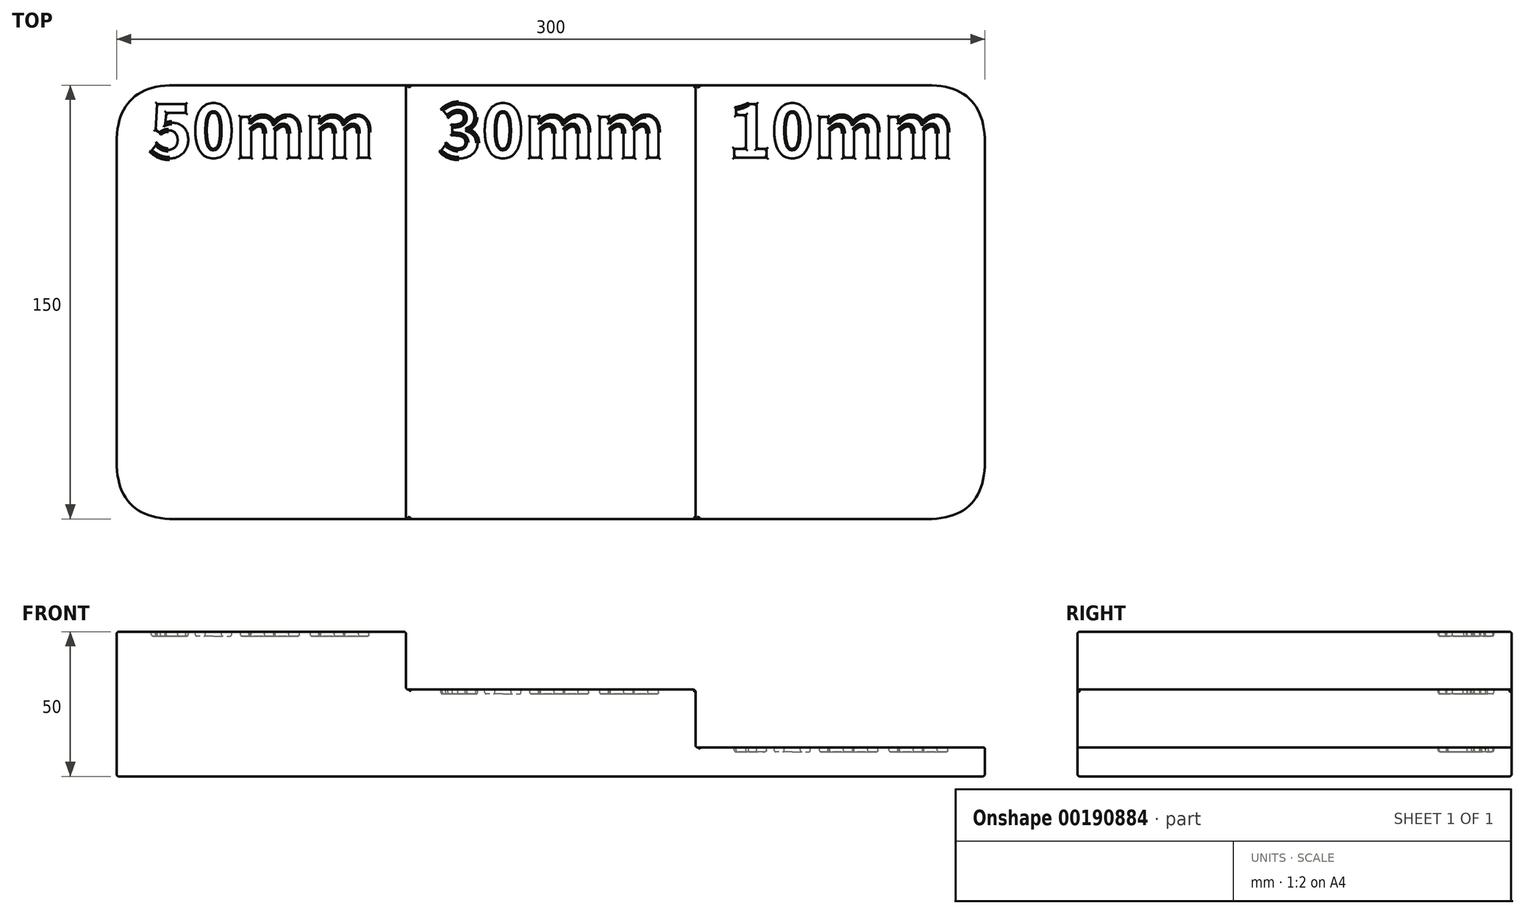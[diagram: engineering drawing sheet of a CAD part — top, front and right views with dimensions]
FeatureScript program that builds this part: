
annotation { "Feature Type Name" : "Feature", "Feature Type Description" : "" }
export const myFeature = defineFeature(function(context is Context, id is Id, definition is map)
    precondition{}
    {
        {
            var Q0;
            Q0=qCreatedBy(makeId("Top.planeOp"),FACE);
            var sketch = newSketch(context, id + "F0", { "sketchPlane" : qUnion([Q0])});
            skLineSegment(sketch, "E0.bottom", {"start": v(150, 75) * mm, "end": v(-150, 75) * mm});
            skLineSegment(sketch, "E0.top", {"start": v(150, -75) * mm, "end": v(-150, -75) * mm});
            skLineSegment(sketch, "E0.left", {"start": v(150, 75) * mm, "end": v(150, -75) * mm});
            skLineSegment(sketch, "E0.right", {"start": v(-150, 75) * mm, "end": v(-150, -75) * mm});
            skPoint(sketch, "E0.middle", {"position": v(0, 0) * mm});
            skLineSegment(sketch, "E1", {"start": v(-150, 0) * mm, "end": v(-50, 0) * mm, "construction": true});
            skLineSegment(sketch, "E2", {"start": v(-50, 0) * mm, "end": v(50, 0) * mm, "construction": true});
            skLineSegment(sketch, "E3", {"start": v(50, 0) * mm, "end": v(150, 0) * mm, "construction": true});
            skLineSegment(sketch, "E4", {"start": v(-50, 75) * mm, "end": v(-50, -75) * mm});
            skLineSegment(sketch, "E5", {"start": v(50, 75) * mm, "end": v(50, -75) * mm});
            skSolve(sketch);
        }
        {
            var Q0;
            Q0 = qSketchRegion(id + "F0", true);
            extrude(context, id + "F1", {"entities" : qUnion([Q0]), "depth" : 10 * mm});
        }
        {
            var Q0;
            {var subQ0=sQuery(id+"F0.wireOp",EDGE,"E4");Q0=makeQuery(id+"F0.imprint","IMPRINT",FACE,{"disambiguationData":[TD([[makeQuery(id+"F0.imprint","IMPRINT",EDGE,{"derivedFrom":subQ0}),1.0]])]});}
            var Q1;
            {var subQ0=sQuery(id+"F0.wireOp",EDGE,"E0.right");Q1=makeQuery(id+"F0.imprint","IMPRINT",FACE,{"disambiguationData":[TD([[makeQuery(id+"F0.imprint","IMPRINT",EDGE,{"derivedFrom":subQ0}),1.0]])]});}
            extrude(context, id + "F2", {"entities" : qUnion([Q0, Q1]), "operationType" : NewBodyOperationType.ADD, "depth" : 30 * mm});
        }
        {
            var Q0;
            {var subQ0=sQuery(id+"F0.wireOp",EDGE,"E0.right");Q0=makeQuery(id+"F0.imprint","IMPRINT",FACE,{"disambiguationData":[TD([[makeQuery(id+"F0.imprint","IMPRINT",EDGE,{"derivedFrom":subQ0}),1.0]])]});}
            extrude(context, id + "F3", {"entities" : qUnion([Q0]), "operationType" : NewBodyOperationType.ADD, "depth" : 50 * mm});
        }
        {
            var Q0;
            {var subQ0=sQuery(id+"F0.wireOp",EDGE,"E0.right");var subQ1=sQuery(id+"F0.wireOp",EDGE,"E0.bottom");Q0=makeQuery(id+"F3.boolean.opBoolean","MERGE",EDGE,{"derivedFrom":[makeQuery(id+"F2.boolean.opBoolean","MERGE",EDGE,{"derivedFrom":[makeQuery(id+"F1.opExtrude","SWEPT_EDGE",EDGE,{"disambiguationData":[OSD([subQ1,subQ0])]}),makeQuery(id+"F2.opExtrude","SWEPT_EDGE",EDGE,{"disambiguationData":[OSD([subQ1,subQ0])]})]}),makeQuery(id+"F3.opExtrude","SWEPT_EDGE",EDGE,{"disambiguationData":[OSD([subQ1,subQ0])]})]});}
            var Q1;
            {var subQ0=sQuery(id+"F0.wireOp",EDGE,"E0.right");var subQ1=sQuery(id+"F0.wireOp",EDGE,"E0.top");Q1=makeQuery(id+"F3.boolean.opBoolean","MERGE",EDGE,{"derivedFrom":[makeQuery(id+"F2.boolean.opBoolean","MERGE",EDGE,{"derivedFrom":[makeQuery(id+"F1.opExtrude","SWEPT_EDGE",EDGE,{"disambiguationData":[OSD([subQ1,subQ0])]}),makeQuery(id+"F2.opExtrude","SWEPT_EDGE",EDGE,{"disambiguationData":[OSD([subQ1,subQ0])]})]}),makeQuery(id+"F3.opExtrude","SWEPT_EDGE",EDGE,{"disambiguationData":[OSD([subQ1,subQ0])]})]});}
            var Q2;
            Q2=makeQuery(id+"F1.opExtrude","SWEPT_EDGE",EDGE,{"disambiguationData":[OSD([sQuery(id+"F0.wireOp",EDGE,"E0.top"),sQuery(id+"F0.wireOp",EDGE,"E0.left")])]});
            var Q3;
            Q3=makeQuery(id+"F1.opExtrude","SWEPT_EDGE",EDGE,{"disambiguationData":[OSD([sQuery(id+"F0.wireOp",EDGE,"E0.bottom"),sQuery(id+"F0.wireOp",EDGE,"E0.left")])]});
            fillet(context, id + "F4", {"entities" : qUnion([Q0, Q1, Q2, Q3]), "radius" : 20 * mm, "tangentPropagation" : true, "rho" : 0.5, "crossSection" : FilletCrossSection.CONIC, "allowEdgeOverflow" : false});
        }
        {
            var Q0;
            {var subQ0=sQuery(id+"F0.wireOp",EDGE,"E0.right");Q0=makeQuery(id+"F3.boolean.opBoolean","MERGE",FACE,{"derivedFrom":[makeQuery(id+"F2.boolean.opBoolean","MERGE",FACE,{"derivedFrom":[makeQuery(id+"F1.opExtrude","SWEPT_FACE",FACE,{"disambiguationData":[OSD([subQ0])]}),makeQuery(id+"F2.opExtrude","SWEPT_FACE",FACE,{"disambiguationData":[OSD([subQ0])]})]}),makeQuery(id+"F3.opExtrude","SWEPT_FACE",FACE,{"disambiguationData":[OSD([subQ0])]})]});}
            var Q1;
            Q1=makeQuery(id+"F3.opExtrude","SWEPT_FACE",FACE,{"disambiguationData":[OSD([sQuery(id+"F0.wireOp",EDGE,"E4")])]});
            var Q2;
            Q2=makeQuery(id+"F2.opExtrude","SWEPT_FACE",FACE,{"disambiguationData":[OSD([sQuery(id+"F0.wireOp",EDGE,"E5")])]});
            fillet(context, id + "F5", {"entities" : qUnion([Q0, Q1, Q2]), "radius" : 0.75 * mm, "tangentPropagation" : true, "allowEdgeOverflow" : false});
        }
        {
            var Q0;
            Q0=makeQuery(id+"F1.opExtrude","CAP_FACE",FACE,{"disambiguationData":[OSD([sQuery(id+"F0.wireOp",EDGE,"E0.bottom"),sQuery(id+"F0.wireOp",EDGE,"E0.top"),sQuery(id+"F0.wireOp",EDGE,"E0.left"),sQuery(id+"F0.wireOp",EDGE,"E0.right")])],"isStart":false});
            var sketch = newSketch(context, id + "F6", { "sketchPlane" : qUnion([Q0])});
            skText(sketch, "E6", { "text": "10mm", "fontName": "NotoSansCJKsc-Bold.otf"});
            skPoint(sketch, "E7", {"position": v(100, 0) * mm});
            const initialGuessF6  = {"E6": [0.06138, 0.05, 1, 0, 0.018]};
            skSetInitialGuess(sketch, initialGuessF6);
            skSolve(sketch);
        }
        {
            var Q0;
            Q0=makeQuery(id+"F2.opExtrude","CAP_FACE",FACE,{"disambiguationData":[OSD([sQuery(id+"F0.wireOp",EDGE,"E0.bottom"),sQuery(id+"F0.wireOp",EDGE,"E0.top"),sQuery(id+"F0.wireOp",EDGE,"E0.right"),sQuery(id+"F0.wireOp",EDGE,"E5")])],"isStart":false});
            var sketch = newSketch(context, id + "F7", { "sketchPlane" : qUnion([Q0])});
            skText(sketch, "E8", { "text": "30mm", "fontName": "NotoSansCJKsc-Bold.otf"});
            skPoint(sketch, "E9", {"position": v(0, 0) * mm});
            const initialGuessF7  = {"E8": [-0.03862, 0.05, 1, 0, 0.018]};
            skSetInitialGuess(sketch, initialGuessF7);
            skSolve(sketch);
        }
        {
            var Q0;
            Q0=makeQuery(id+"F3.opExtrude","CAP_FACE",FACE,{"disambiguationData":[OSD([sQuery(id+"F0.wireOp",EDGE,"E0.bottom"),sQuery(id+"F0.wireOp",EDGE,"E0.top"),sQuery(id+"F0.wireOp",EDGE,"E0.right"),sQuery(id+"F0.wireOp",EDGE,"E4")])],"isStart":false});
            var sketch = newSketch(context, id + "F8", { "sketchPlane" : qUnion([Q0])});
            skText(sketch, "E10", { "text": "50mm", "fontName": "NotoSansCJKsc-Bold.otf"});
            skPoint(sketch, "E11", {"position": v(-100, 0) * mm});
            const initialGuessF8  = {"E10": [-0.13862, 0.05, 1, 0, 0.018]};
            skSetInitialGuess(sketch, initialGuessF8);
            skSolve(sketch);
        }
        {
            var Q0;
            Q0 = qSketchRegion(id + "F6", true);
            var Q1;
            Q1 = qSketchRegion(id + "F7", true);
            var Q2;
            Q2 = qSketchRegion(id + "F8", true);
            extrude(context, id + "F9", {"entities" : qUnion([Q0, Q1, Q2]), "operationType" : NewBodyOperationType.REMOVE, "oppositeDirection" : true, "depth" : 1.5 * mm});
        }
        {
            var Q0;
            {var subQ0=sQuery(id+"F0.wireOp",EDGE,"E0.right");var subQ1=sQuery(id+"F0.wireOp",EDGE,"E0.left");var subQ2=sQuery(id+"F0.wireOp",EDGE,"E0.top");var subQ3=sQuery(id+"F0.wireOp",EDGE,"E0.bottom");var subQ4=makeQuery(id+"F1.opExtrude","CAP_FACE",FACE,{"disambiguationData":[OSD([subQ3,subQ2,subQ1,subQ0])],"isStart":false});var subQ5=subQ4;Q0=makeQuery(id+"F9.boolean.opBoolean","SPLIT",FACE,{"disambiguationData":[TD([makeQuery(id+"F9.opExtrude","SWEPT_FACE",FACE,{"disambiguationData":[OSD([sQuery(id+"F6.wireOp",EDGE,"E6.sketch_text.stroke-0")])]})])],"derivedFrom":subQ5});}
            var Q1;
            Q1=makeQuery(id+"F9.boolean.opBoolean","SPLIT",FACE,{"disambiguationData":[TD([makeQuery(id+"F9.opExtrude","SWEPT_FACE",FACE,{"disambiguationData":[OSD([sQuery(id+"F6.wireOp",EDGE,"E6.sketch_text.stroke-15")])]})])],"derivedFrom":makeQuery(id+"F1.opExtrude","CAP_FACE",FACE,{"disambiguationData":[OSD([sQuery(id+"F0.wireOp",EDGE,"E0.bottom"),sQuery(id+"F0.wireOp",EDGE,"E0.top"),sQuery(id+"F0.wireOp",EDGE,"E0.left"),sQuery(id+"F0.wireOp",EDGE,"E0.right")])],"isStart":false})});
            var Q2;
            Q2=makeQuery(id+"F9.boolean.opBoolean","COPY",FACE,{"derivedFrom":makeQuery(id+"F9.opExtrude","CAP_FACE",FACE,{"disambiguationData":[OSD([sQuery(id+"F6.wireOp",EDGE,"E6.sketch_text.stroke-0"),sQuery(id+"F6.wireOp",EDGE,"E6.sketch_text.stroke-1"),sQuery(id+"F6.wireOp",EDGE,"E6.sketch_text.stroke-2"),sQuery(id+"F6.wireOp",EDGE,"E6.sketch_text.stroke-3"),sQuery(id+"F6.wireOp",EDGE,"E6.sketch_text.stroke-4"),sQuery(id+"F6.wireOp",EDGE,"E6.sketch_text.stroke-5"),sQuery(id+"F6.wireOp",EDGE,"E6.sketch_text.stroke-6"),sQuery(id+"F6.wireOp",EDGE,"E6.sketch_text.stroke-7"),sQuery(id+"F6.wireOp",EDGE,"E6.sketch_text.stroke-8"),sQuery(id+"F6.wireOp",EDGE,"E6.sketch_text.stroke-9"),sQuery(id+"F6.wireOp",EDGE,"E6.sketch_text.stroke-10")])],"isStart":false})});
            var Q3;
            Q3=makeQuery(id+"F9.boolean.opBoolean","COPY",FACE,{"derivedFrom":makeQuery(id+"F9.opExtrude","CAP_FACE",FACE,{"disambiguationData":[OSD([sQuery(id+"F6.wireOp",EDGE,"E6.sketch_text.stroke-11"),sQuery(id+"F6.wireOp",EDGE,"E6.sketch_text.stroke-12"),sQuery(id+"F6.wireOp",EDGE,"E6.sketch_text.stroke-13"),sQuery(id+"F6.wireOp",EDGE,"E6.sketch_text.stroke-14"),sQuery(id+"F6.wireOp",EDGE,"E6.sketch_text.stroke-15"),sQuery(id+"F6.wireOp",EDGE,"E6.sketch_text.stroke-16"),sQuery(id+"F6.wireOp",EDGE,"E6.sketch_text.stroke-17"),sQuery(id+"F6.wireOp",EDGE,"E6.sketch_text.stroke-18")])],"isStart":false})});
            var Q4;
            Q4=makeQuery(id+"F9.boolean.opBoolean","COPY",FACE,{"derivedFrom":makeQuery(id+"F9.opExtrude","CAP_FACE",FACE,{"disambiguationData":[OSD([sQuery(id+"F6.wireOp",EDGE,"E6.sketch_text.stroke-19"),sQuery(id+"F6.wireOp",EDGE,"E6.sketch_text.stroke-20"),sQuery(id+"F6.wireOp",EDGE,"E6.sketch_text.stroke-21"),sQuery(id+"F6.wireOp",EDGE,"E6.sketch_text.stroke-22"),sQuery(id+"F6.wireOp",EDGE,"E6.sketch_text.stroke-23"),sQuery(id+"F6.wireOp",EDGE,"E6.sketch_text.stroke-24"),sQuery(id+"F6.wireOp",EDGE,"E6.sketch_text.stroke-25"),sQuery(id+"F6.wireOp",EDGE,"E6.sketch_text.stroke-26"),sQuery(id+"F6.wireOp",EDGE,"E6.sketch_text.stroke-27"),sQuery(id+"F6.wireOp",EDGE,"E6.sketch_text.stroke-28"),sQuery(id+"F6.wireOp",EDGE,"E6.sketch_text.stroke-29"),sQuery(id+"F6.wireOp",EDGE,"E6.sketch_text.stroke-30"),sQuery(id+"F6.wireOp",EDGE,"E6.sketch_text.stroke-31"),sQuery(id+"F6.wireOp",EDGE,"E6.sketch_text.stroke-32"),sQuery(id+"F6.wireOp",EDGE,"E6.sketch_text.stroke-33"),sQuery(id+"F6.wireOp",EDGE,"E6.sketch_text.stroke-34"),sQuery(id+"F6.wireOp",EDGE,"E6.sketch_text.stroke-35"),sQuery(id+"F6.wireOp",EDGE,"E6.sketch_text.stroke-36"),sQuery(id+"F6.wireOp",EDGE,"E6.sketch_text.stroke-37"),sQuery(id+"F6.wireOp",EDGE,"E6.sketch_text.stroke-38")])],"isStart":false})});
            var Q5;
            Q5=makeQuery(id+"F9.boolean.opBoolean","COPY",FACE,{"derivedFrom":makeQuery(id+"F9.opExtrude","CAP_FACE",FACE,{"disambiguationData":[OSD([sQuery(id+"F6.wireOp",EDGE,"E6.sketch_text.stroke-39"),sQuery(id+"F6.wireOp",EDGE,"E6.sketch_text.stroke-40"),sQuery(id+"F6.wireOp",EDGE,"E6.sketch_text.stroke-41"),sQuery(id+"F6.wireOp",EDGE,"E6.sketch_text.stroke-42"),sQuery(id+"F6.wireOp",EDGE,"E6.sketch_text.stroke-43"),sQuery(id+"F6.wireOp",EDGE,"E6.sketch_text.stroke-44"),sQuery(id+"F6.wireOp",EDGE,"E6.sketch_text.stroke-45"),sQuery(id+"F6.wireOp",EDGE,"E6.sketch_text.stroke-46"),sQuery(id+"F6.wireOp",EDGE,"E6.sketch_text.stroke-47"),sQuery(id+"F6.wireOp",EDGE,"E6.sketch_text.stroke-48"),sQuery(id+"F6.wireOp",EDGE,"E6.sketch_text.stroke-49"),sQuery(id+"F6.wireOp",EDGE,"E6.sketch_text.stroke-50"),sQuery(id+"F6.wireOp",EDGE,"E6.sketch_text.stroke-51"),sQuery(id+"F6.wireOp",EDGE,"E6.sketch_text.stroke-52"),sQuery(id+"F6.wireOp",EDGE,"E6.sketch_text.stroke-53"),sQuery(id+"F6.wireOp",EDGE,"E6.sketch_text.stroke-54"),sQuery(id+"F6.wireOp",EDGE,"E6.sketch_text.stroke-55"),sQuery(id+"F6.wireOp",EDGE,"E6.sketch_text.stroke-56"),sQuery(id+"F6.wireOp",EDGE,"E6.sketch_text.stroke-57"),sQuery(id+"F6.wireOp",EDGE,"E6.sketch_text.stroke-58")])],"isStart":false})});
            var Q6;
            {var subQ0=sQuery(id+"F0.wireOp",EDGE,"E0.top");var subQ3=sQuery(id+"F0.wireOp",EDGE,"E5");var subQ4=sQuery(id+"F0.wireOp",EDGE,"E0.right");var subQ5=sQuery(id+"F0.wireOp",EDGE,"E0.bottom");var subQ6=makeQuery(id+"F2.opExtrude","CAP_FACE",FACE,{"disambiguationData":[OSD([subQ5,subQ0,subQ4,subQ3])],"isStart":false});Q6=makeQuery(id+"F9.boolean.opBoolean","SPLIT",FACE,{"disambiguationData":[TD([makeQuery(id+"F5.opFillet","BLEND_FACE",FACE,{"disambiguationData":[OSD([subQ3])]})])],"derivedFrom":subQ6});}
            var Q7;
            Q7=makeQuery(id+"F9.boolean.opBoolean","SPLIT",FACE,{"disambiguationData":[TD([makeQuery(id+"F9.opExtrude","SWEPT_FACE",FACE,{"disambiguationData":[OSD([sQuery(id+"F7.wireOp",EDGE,"E8.sketch_text.stroke-20")])]})])],"derivedFrom":makeQuery(id+"F2.opExtrude","CAP_FACE",FACE,{"disambiguationData":[OSD([sQuery(id+"F0.wireOp",EDGE,"E0.bottom"),sQuery(id+"F0.wireOp",EDGE,"E0.top"),sQuery(id+"F0.wireOp",EDGE,"E0.right"),sQuery(id+"F0.wireOp",EDGE,"E5")])],"isStart":false})});
            var Q8;
            Q8=makeQuery(id+"F9.boolean.opBoolean","COPY",FACE,{"derivedFrom":makeQuery(id+"F9.opExtrude","CAP_FACE",FACE,{"disambiguationData":[OSD([sQuery(id+"F7.wireOp",EDGE,"E8.sketch_text.stroke-0"),sQuery(id+"F7.wireOp",EDGE,"E8.sketch_text.stroke-1"),sQuery(id+"F7.wireOp",EDGE,"E8.sketch_text.stroke-2"),sQuery(id+"F7.wireOp",EDGE,"E8.sketch_text.stroke-3"),sQuery(id+"F7.wireOp",EDGE,"E8.sketch_text.stroke-4"),sQuery(id+"F7.wireOp",EDGE,"E8.sketch_text.stroke-5"),sQuery(id+"F7.wireOp",EDGE,"E8.sketch_text.stroke-6"),sQuery(id+"F7.wireOp",EDGE,"E8.sketch_text.stroke-7"),sQuery(id+"F7.wireOp",EDGE,"E8.sketch_text.stroke-8"),sQuery(id+"F7.wireOp",EDGE,"E8.sketch_text.stroke-9"),sQuery(id+"F7.wireOp",EDGE,"E8.sketch_text.stroke-10"),sQuery(id+"F7.wireOp",EDGE,"E8.sketch_text.stroke-11"),sQuery(id+"F7.wireOp",EDGE,"E8.sketch_text.stroke-12"),sQuery(id+"F7.wireOp",EDGE,"E8.sketch_text.stroke-13"),sQuery(id+"F7.wireOp",EDGE,"E8.sketch_text.stroke-14"),sQuery(id+"F7.wireOp",EDGE,"E8.sketch_text.stroke-15")])],"isStart":false})});
            var Q9;
            Q9=makeQuery(id+"F9.boolean.opBoolean","COPY",FACE,{"derivedFrom":makeQuery(id+"F9.opExtrude","CAP_FACE",FACE,{"disambiguationData":[OSD([sQuery(id+"F7.wireOp",EDGE,"E8.sketch_text.stroke-16"),sQuery(id+"F7.wireOp",EDGE,"E8.sketch_text.stroke-17"),sQuery(id+"F7.wireOp",EDGE,"E8.sketch_text.stroke-18"),sQuery(id+"F7.wireOp",EDGE,"E8.sketch_text.stroke-19"),sQuery(id+"F7.wireOp",EDGE,"E8.sketch_text.stroke-20"),sQuery(id+"F7.wireOp",EDGE,"E8.sketch_text.stroke-21"),sQuery(id+"F7.wireOp",EDGE,"E8.sketch_text.stroke-22"),sQuery(id+"F7.wireOp",EDGE,"E8.sketch_text.stroke-23")])],"isStart":false})});
            var Q10;
            Q10=makeQuery(id+"F9.boolean.opBoolean","COPY",FACE,{"derivedFrom":makeQuery(id+"F9.opExtrude","CAP_FACE",FACE,{"disambiguationData":[OSD([sQuery(id+"F7.wireOp",EDGE,"E8.sketch_text.stroke-24"),sQuery(id+"F7.wireOp",EDGE,"E8.sketch_text.stroke-25"),sQuery(id+"F7.wireOp",EDGE,"E8.sketch_text.stroke-26"),sQuery(id+"F7.wireOp",EDGE,"E8.sketch_text.stroke-27"),sQuery(id+"F7.wireOp",EDGE,"E8.sketch_text.stroke-28"),sQuery(id+"F7.wireOp",EDGE,"E8.sketch_text.stroke-29"),sQuery(id+"F7.wireOp",EDGE,"E8.sketch_text.stroke-30"),sQuery(id+"F7.wireOp",EDGE,"E8.sketch_text.stroke-31"),sQuery(id+"F7.wireOp",EDGE,"E8.sketch_text.stroke-32"),sQuery(id+"F7.wireOp",EDGE,"E8.sketch_text.stroke-33"),sQuery(id+"F7.wireOp",EDGE,"E8.sketch_text.stroke-34"),sQuery(id+"F7.wireOp",EDGE,"E8.sketch_text.stroke-35"),sQuery(id+"F7.wireOp",EDGE,"E8.sketch_text.stroke-36"),sQuery(id+"F7.wireOp",EDGE,"E8.sketch_text.stroke-37"),sQuery(id+"F7.wireOp",EDGE,"E8.sketch_text.stroke-38"),sQuery(id+"F7.wireOp",EDGE,"E8.sketch_text.stroke-39"),sQuery(id+"F7.wireOp",EDGE,"E8.sketch_text.stroke-40"),sQuery(id+"F7.wireOp",EDGE,"E8.sketch_text.stroke-41"),sQuery(id+"F7.wireOp",EDGE,"E8.sketch_text.stroke-42"),sQuery(id+"F7.wireOp",EDGE,"E8.sketch_text.stroke-43")])],"isStart":false})});
            var Q11;
            Q11=makeQuery(id+"F9.boolean.opBoolean","COPY",FACE,{"derivedFrom":makeQuery(id+"F9.opExtrude","CAP_FACE",FACE,{"disambiguationData":[OSD([sQuery(id+"F7.wireOp",EDGE,"E8.sketch_text.stroke-44"),sQuery(id+"F7.wireOp",EDGE,"E8.sketch_text.stroke-45"),sQuery(id+"F7.wireOp",EDGE,"E8.sketch_text.stroke-46"),sQuery(id+"F7.wireOp",EDGE,"E8.sketch_text.stroke-47"),sQuery(id+"F7.wireOp",EDGE,"E8.sketch_text.stroke-48"),sQuery(id+"F7.wireOp",EDGE,"E8.sketch_text.stroke-49"),sQuery(id+"F7.wireOp",EDGE,"E8.sketch_text.stroke-50"),sQuery(id+"F7.wireOp",EDGE,"E8.sketch_text.stroke-51"),sQuery(id+"F7.wireOp",EDGE,"E8.sketch_text.stroke-52"),sQuery(id+"F7.wireOp",EDGE,"E8.sketch_text.stroke-53"),sQuery(id+"F7.wireOp",EDGE,"E8.sketch_text.stroke-54"),sQuery(id+"F7.wireOp",EDGE,"E8.sketch_text.stroke-55"),sQuery(id+"F7.wireOp",EDGE,"E8.sketch_text.stroke-56"),sQuery(id+"F7.wireOp",EDGE,"E8.sketch_text.stroke-57"),sQuery(id+"F7.wireOp",EDGE,"E8.sketch_text.stroke-58"),sQuery(id+"F7.wireOp",EDGE,"E8.sketch_text.stroke-59"),sQuery(id+"F7.wireOp",EDGE,"E8.sketch_text.stroke-60"),sQuery(id+"F7.wireOp",EDGE,"E8.sketch_text.stroke-61"),sQuery(id+"F7.wireOp",EDGE,"E8.sketch_text.stroke-62"),sQuery(id+"F7.wireOp",EDGE,"E8.sketch_text.stroke-63")])],"isStart":false})});
            var Q12;
            {var subQ0=sQuery(id+"F0.wireOp",EDGE,"E4");var subQ1=sQuery(id+"F0.wireOp",EDGE,"E0.right");var subQ2=sQuery(id+"F0.wireOp",EDGE,"E0.top");var subQ3=sQuery(id+"F0.wireOp",EDGE,"E0.bottom");var subQ4=makeQuery(id+"F3.opExtrude","CAP_FACE",FACE,{"disambiguationData":[OSD([subQ3,subQ2,subQ1,subQ0])],"isStart":false});Q12=makeQuery(id+"F9.boolean.opBoolean","SPLIT",FACE,{"disambiguationData":[TD([makeQuery(id+"F5.opFillet","BLEND_FACE",FACE,{"disambiguationData":[OSD([subQ0])]})])],"derivedFrom":subQ4});}
            var Q13;
            Q13=makeQuery(id+"F9.boolean.opBoolean","SPLIT",FACE,{"disambiguationData":[TD([makeQuery(id+"F9.opExtrude","SWEPT_FACE",FACE,{"disambiguationData":[OSD([sQuery(id+"F8.wireOp",EDGE,"E10.sketch_text.stroke-19")])]})])],"derivedFrom":makeQuery(id+"F3.opExtrude","CAP_FACE",FACE,{"disambiguationData":[OSD([sQuery(id+"F0.wireOp",EDGE,"E0.bottom"),sQuery(id+"F0.wireOp",EDGE,"E0.top"),sQuery(id+"F0.wireOp",EDGE,"E0.right"),sQuery(id+"F0.wireOp",EDGE,"E4")])],"isStart":false})});
            var Q14;
            Q14=makeQuery(id+"F9.boolean.opBoolean","COPY",FACE,{"derivedFrom":makeQuery(id+"F9.opExtrude","CAP_FACE",FACE,{"disambiguationData":[OSD([sQuery(id+"F8.wireOp",EDGE,"E10.sketch_text.stroke-0"),sQuery(id+"F8.wireOp",EDGE,"E10.sketch_text.stroke-1"),sQuery(id+"F8.wireOp",EDGE,"E10.sketch_text.stroke-2"),sQuery(id+"F8.wireOp",EDGE,"E10.sketch_text.stroke-3"),sQuery(id+"F8.wireOp",EDGE,"E10.sketch_text.stroke-4"),sQuery(id+"F8.wireOp",EDGE,"E10.sketch_text.stroke-5"),sQuery(id+"F8.wireOp",EDGE,"E10.sketch_text.stroke-6"),sQuery(id+"F8.wireOp",EDGE,"E10.sketch_text.stroke-7"),sQuery(id+"F8.wireOp",EDGE,"E10.sketch_text.stroke-8"),sQuery(id+"F8.wireOp",EDGE,"E10.sketch_text.stroke-9"),sQuery(id+"F8.wireOp",EDGE,"E10.sketch_text.stroke-10"),sQuery(id+"F8.wireOp",EDGE,"E10.sketch_text.stroke-11"),sQuery(id+"F8.wireOp",EDGE,"E10.sketch_text.stroke-12"),sQuery(id+"F8.wireOp",EDGE,"E10.sketch_text.stroke-13"),sQuery(id+"F8.wireOp",EDGE,"E10.sketch_text.stroke-14")])],"isStart":false})});
            var Q15;
            Q15=makeQuery(id+"F9.boolean.opBoolean","COPY",FACE,{"derivedFrom":makeQuery(id+"F9.opExtrude","CAP_FACE",FACE,{"disambiguationData":[OSD([sQuery(id+"F8.wireOp",EDGE,"E10.sketch_text.stroke-15"),sQuery(id+"F8.wireOp",EDGE,"E10.sketch_text.stroke-16"),sQuery(id+"F8.wireOp",EDGE,"E10.sketch_text.stroke-17"),sQuery(id+"F8.wireOp",EDGE,"E10.sketch_text.stroke-18"),sQuery(id+"F8.wireOp",EDGE,"E10.sketch_text.stroke-19"),sQuery(id+"F8.wireOp",EDGE,"E10.sketch_text.stroke-20"),sQuery(id+"F8.wireOp",EDGE,"E10.sketch_text.stroke-21"),sQuery(id+"F8.wireOp",EDGE,"E10.sketch_text.stroke-22")])],"isStart":false})});
            var Q16;
            Q16=makeQuery(id+"F9.boolean.opBoolean","COPY",FACE,{"derivedFrom":makeQuery(id+"F9.opExtrude","CAP_FACE",FACE,{"disambiguationData":[OSD([sQuery(id+"F8.wireOp",EDGE,"E10.sketch_text.stroke-23"),sQuery(id+"F8.wireOp",EDGE,"E10.sketch_text.stroke-24"),sQuery(id+"F8.wireOp",EDGE,"E10.sketch_text.stroke-25"),sQuery(id+"F8.wireOp",EDGE,"E10.sketch_text.stroke-26"),sQuery(id+"F8.wireOp",EDGE,"E10.sketch_text.stroke-27"),sQuery(id+"F8.wireOp",EDGE,"E10.sketch_text.stroke-28"),sQuery(id+"F8.wireOp",EDGE,"E10.sketch_text.stroke-29"),sQuery(id+"F8.wireOp",EDGE,"E10.sketch_text.stroke-30"),sQuery(id+"F8.wireOp",EDGE,"E10.sketch_text.stroke-31"),sQuery(id+"F8.wireOp",EDGE,"E10.sketch_text.stroke-32"),sQuery(id+"F8.wireOp",EDGE,"E10.sketch_text.stroke-33"),sQuery(id+"F8.wireOp",EDGE,"E10.sketch_text.stroke-34"),sQuery(id+"F8.wireOp",EDGE,"E10.sketch_text.stroke-35"),sQuery(id+"F8.wireOp",EDGE,"E10.sketch_text.stroke-36"),sQuery(id+"F8.wireOp",EDGE,"E10.sketch_text.stroke-37"),sQuery(id+"F8.wireOp",EDGE,"E10.sketch_text.stroke-38"),sQuery(id+"F8.wireOp",EDGE,"E10.sketch_text.stroke-39"),sQuery(id+"F8.wireOp",EDGE,"E10.sketch_text.stroke-40"),sQuery(id+"F8.wireOp",EDGE,"E10.sketch_text.stroke-41"),sQuery(id+"F8.wireOp",EDGE,"E10.sketch_text.stroke-42")])],"isStart":false})});
            var Q17;
            Q17=makeQuery(id+"F9.boolean.opBoolean","COPY",FACE,{"derivedFrom":makeQuery(id+"F9.opExtrude","CAP_FACE",FACE,{"disambiguationData":[OSD([sQuery(id+"F8.wireOp",EDGE,"E10.sketch_text.stroke-43"),sQuery(id+"F8.wireOp",EDGE,"E10.sketch_text.stroke-44"),sQuery(id+"F8.wireOp",EDGE,"E10.sketch_text.stroke-45"),sQuery(id+"F8.wireOp",EDGE,"E10.sketch_text.stroke-46"),sQuery(id+"F8.wireOp",EDGE,"E10.sketch_text.stroke-47"),sQuery(id+"F8.wireOp",EDGE,"E10.sketch_text.stroke-48"),sQuery(id+"F8.wireOp",EDGE,"E10.sketch_text.stroke-49"),sQuery(id+"F8.wireOp",EDGE,"E10.sketch_text.stroke-50"),sQuery(id+"F8.wireOp",EDGE,"E10.sketch_text.stroke-51"),sQuery(id+"F8.wireOp",EDGE,"E10.sketch_text.stroke-52"),sQuery(id+"F8.wireOp",EDGE,"E10.sketch_text.stroke-53"),sQuery(id+"F8.wireOp",EDGE,"E10.sketch_text.stroke-54"),sQuery(id+"F8.wireOp",EDGE,"E10.sketch_text.stroke-55"),sQuery(id+"F8.wireOp",EDGE,"E10.sketch_text.stroke-56"),sQuery(id+"F8.wireOp",EDGE,"E10.sketch_text.stroke-57"),sQuery(id+"F8.wireOp",EDGE,"E10.sketch_text.stroke-58"),sQuery(id+"F8.wireOp",EDGE,"E10.sketch_text.stroke-59"),sQuery(id+"F8.wireOp",EDGE,"E10.sketch_text.stroke-60"),sQuery(id+"F8.wireOp",EDGE,"E10.sketch_text.stroke-61"),sQuery(id+"F8.wireOp",EDGE,"E10.sketch_text.stroke-62")])],"isStart":false})});
            fillet(context, id + "F10", {"entities" : qUnion([Q0, Q1, Q2, Q3, Q4, Q5, Q6, Q7, Q8, Q9, Q10, Q11, Q12, Q13, Q14, Q15, Q16, Q17]), "radius" : 0.5 * mm, "tangentPropagation" : true, "allowEdgeOverflow" : false});
        }
    });
